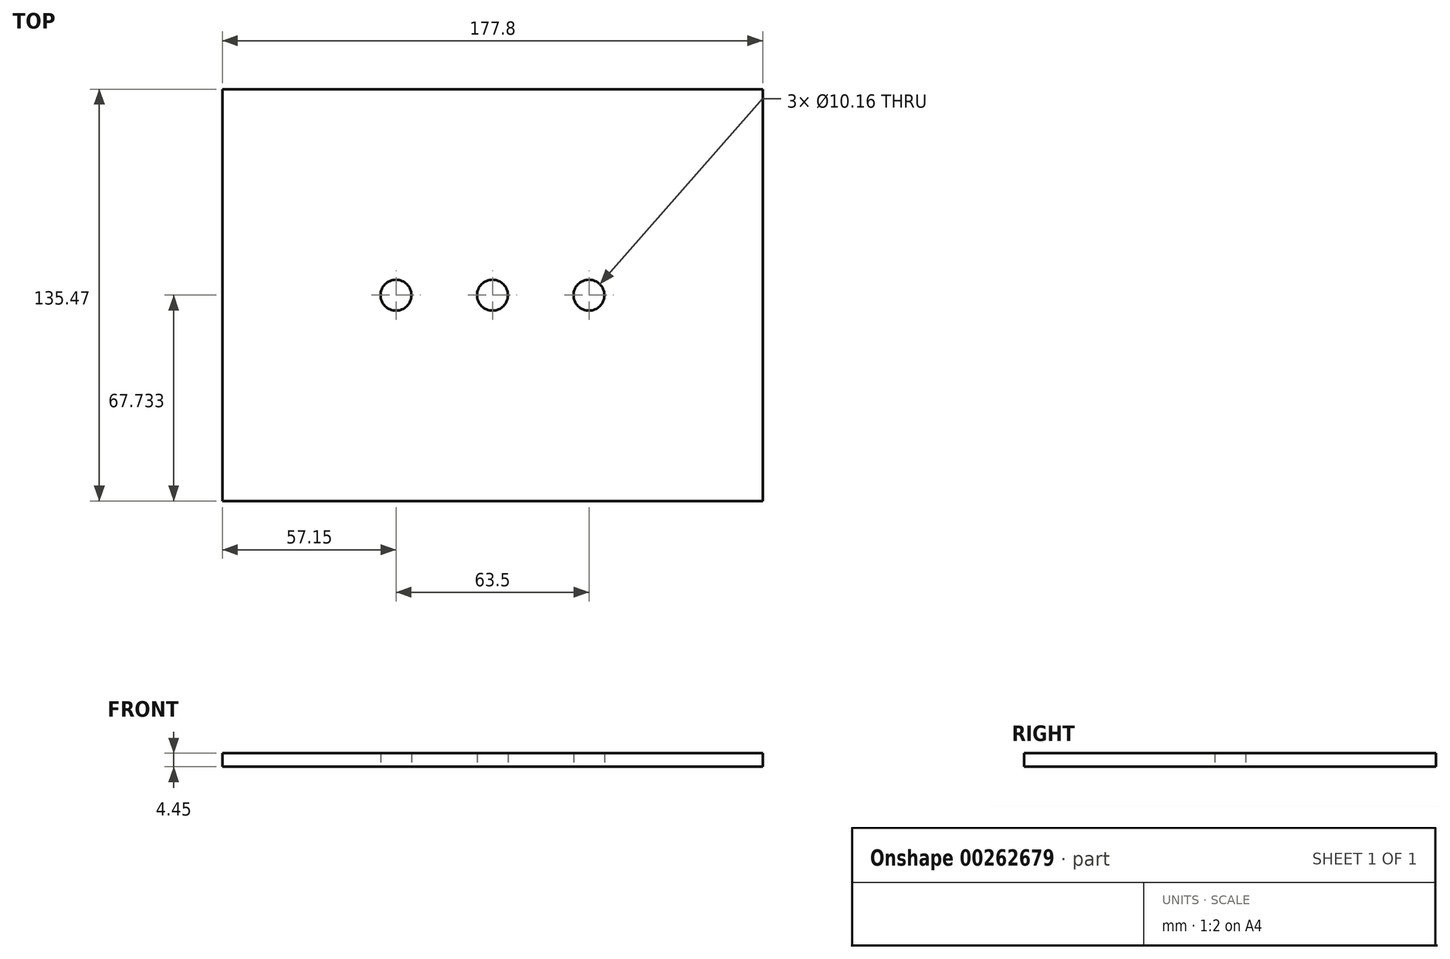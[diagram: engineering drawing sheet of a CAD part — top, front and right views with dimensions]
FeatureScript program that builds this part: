
annotation { "Feature Type Name" : "Feature", "Feature Type Description" : "" }
export const myFeature = defineFeature(function(context is Context, id is Id, definition is map)
    precondition{}
    {
        {
            var Q0;
            Q0=qCreatedBy(makeId("Top.planeOp"),FACE);
            var sketch = newSketch(context, id + "F0", { "sketchPlane" : qUnion([Q0])});
            skLineSegment(sketch, "E0.bottom", {"start": v(0, 0) * mm, "end": v(177.8, 0) * mm});
            skLineSegment(sketch, "E0.top", {"start": v(0, 135.47) * mm, "end": v(177.8, 135.47) * mm});
            skLineSegment(sketch, "E0.left", {"start": v(0, 0) * mm, "end": v(0, 135.47) * mm});
            skLineSegment(sketch, "E0.right", {"start": v(177.8, 0) * mm, "end": v(177.8, 135.47) * mm});
            skCircle(sketch, "E1", {"center": v(57.15, 67.73) * mm, "radius": 5.08 * mm});
            skPoint(sketch, "E1.centerSnap0", {"position": v(0, 67.73) * mm});
            skCircle(sketch, "E2", {"center": v(88.9, 67.73) * mm, "radius": 5.08 * mm});
            skCircle(sketch, "E3", {"center": v(120.65, 67.73) * mm, "radius": 5.08 * mm});
            skSolve(sketch);
        }
        {
            var Q0;
            Q0=makeQuery(id+"F0.imprint","IMPRINT",FACE,{"disambiguationData":[TD([[makeQuery(id+"F0.imprint","IMPRINT",EDGE,{"derivedFrom":sQuery(id+"F0.wireOp",EDGE,"E0.bottom")}),1.0]])]});
            extrude(context, id + "F1", {"entities" : qUnion([Q0]), "depth" : 4.44 * mm});
        }
    });
